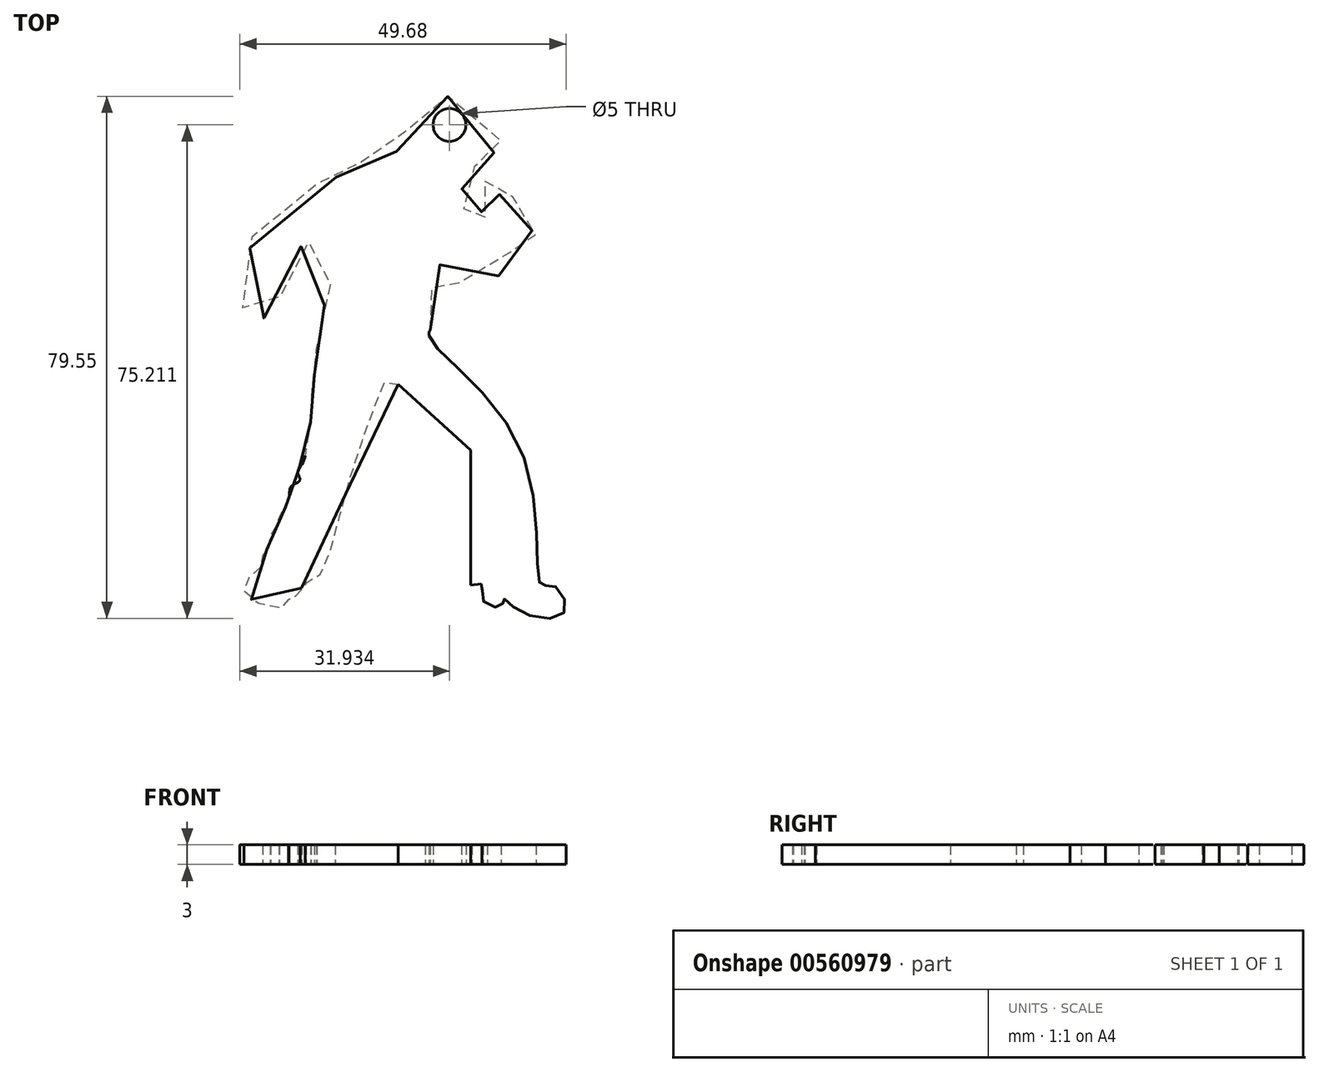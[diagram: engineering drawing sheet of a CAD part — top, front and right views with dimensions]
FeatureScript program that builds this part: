
annotation { "Feature Type Name" : "Feature", "Feature Type Description" : "" }
export const myFeature = defineFeature(function(context is Context, id is Id, definition is map)
    precondition{}
    {
        {
            var Q0;
            Q0=qCreatedBy(makeId("Top.planeOp"),FACE);
            var sketch = newSketch(context, id + "F0", { "sketchPlane" : qUnion([Q0])});
            skFitSpline(sketch, "E0", {"points": [v(7.17, 0) * mm, v(6.71, 2.56) * mm, v(6.74, 3.65) * mm, v(7.82, 7.82) * mm, v(9.38, 11.25) * mm, v(11.99, 7.81) * mm, v(16.18, 6.76) * mm, v(20.58, 14.63) * mm, v(21.9, 13.78) * mm, v(23.5, 14.86) * mm, v(22.16, 16.95) * mm, v(21.52, 20.06) * mm, v(19.31, 21.14) * mm, v(18.2, 20.93) * mm, v(17.4, 22.89) * mm, v(15.1, 23.35) * mm, v(13.71, 21.36) * mm, v(15.27, 18.68) * mm, v(16.02, 16.2) * mm, v(14.6, 15.12) * mm, v(12.27, 22.69) * mm, v(13.55, 23.47) * mm, v(14.08, 25.3) * mm, v(15.4, 27.9) * mm, v(17.46, 27.9) * mm, v(17.99, 30.5) * mm, v(12.78, 35.72) * mm, v(6.52, 35.72) * mm, v(3.65, 31.81) * mm, v(2.08, 27.9) * mm, v(-2.61, 26.34) * mm, v(-5.21, 26.33) * mm, v(-6.78, 24.26) * mm, v(-17.07, 20.47) * mm, v(-20.5, 11.2) * mm, v(-21.56, 5.16) * mm, v(-19.17, 2.55) * mm, v(-15.85, 4.39) * mm, v(-15.12, 9.9) * mm, v(-11.47, 14.08) * mm, v(-7.56, 14.34) * mm, v(-8.5, 5.5) * mm, v(-9.88, 0) * mm, v(-9.9, -2.87) * mm, v(-10.17, -5.74) * mm, v(-10.8, -7.12) * mm, v(-10.3, -9.22) * mm, v(-11.52, -11) * mm, v(-10.89, -12.85) * mm, v(-11.47, -14.34) * mm, v(-12.21, -15.98) * mm, v(-11.74, -17.73) * mm, v(-12, -19.3) * mm, v(-12.8, -20.87) * mm, v(-12.45, -21.96) * mm, v(-13.15, -22.56) * mm, v(-14, -23.38) * mm, v(-14.35, -25.81) * mm, v(-15.55, -26.83) * mm, v(-15.74, -28.8) * mm, v(-16.93, -29.78) * mm, v(-17.05, -32.11) * mm, v(-18.07, -33.1) * mm, v(-18.26, -34.94) * mm, v(-20.6, -37.3) * mm, v(-20.34, -39.89) * mm, v(-14.34, -41.19) * mm, v(-14.08, -39.64) * mm, v(-12.47, -39.64) * mm, v(-12.14, -37.97) * mm, v(-10.16, -37.18) * mm, v(-5.74, -24.94) * mm, v(0, -8.1) * mm, v(2.48, -7.41) * mm], "startDerivative": vector(130.3, 275.78) * mm, "endDerivative": vector(321.5, -506.5) * mm});
            skLineSegment(sketch, "E1", {"start": v(2.48, -7.41) * mm, "end": v(13.56, -17.47) * mm});
            skLineSegment(sketch, "E2", {"start": v(13.56, -17.47) * mm, "end": v(13.56, -38.07) * mm});
            skFitSpline(sketch, "E3", {"points": [v(13.56, -38.07) * mm, v(15.38, -38.07) * mm, v(15.38, -40.42) * mm, v(18.25, -41.2) * mm, v(18.51, -40.16) * mm, v(21.38, -42.24) * mm, v(27.9, -41.98) * mm, v(26.08, -38.07) * mm, v(24.25, -38.07) * mm, v(21.12, -17.21) * mm, v(7.17, 0) * mm, v(7.7, 1.14) * mm], "startDerivative": vector(43.89, 9.96) * mm, "endDerivative": vector(14.45, 9.26) * mm});
            skCircle(sketch, "E4", {"center": v(10.3, 32.1) * mm, "radius": 2.5 * mm});
            skPoint(sketch, "E5", {"position": v(14.48, 19.73) * mm});
            skPoint(sketch, "E6", {"position": v(-2.52, -14.7) * mm});
            skSolve(sketch);
        }
        {
            var Q0;
            {var subQ4=sQuery(id+"F0.wireOp",EDGE,"E1");Q0=makeQuery(id+"F0.imprint","IMPRINT",FACE,{"disambiguationData":[TD([[makeQuery(id+"F0.imprint","IMPRINT",EDGE,{"derivedFrom":subQ4}),1.0]])]});}
            extrude(context, id + "F1", {"entities" : qUnion([Q0]), "depth" : 3 * mm, "offsetDistance" : 25 * mm});
        }
    });
